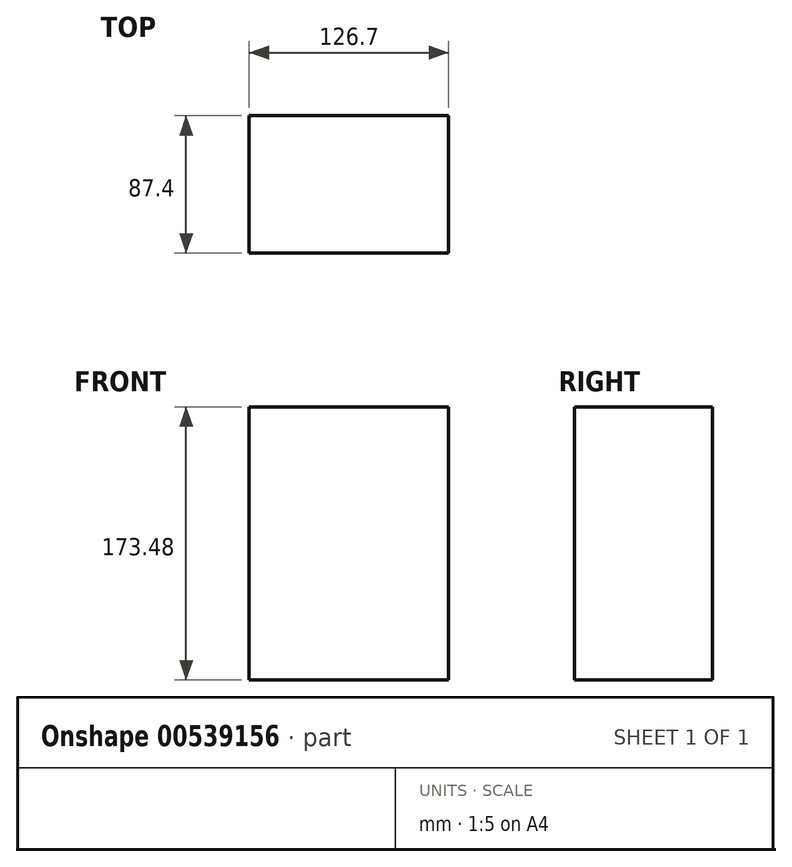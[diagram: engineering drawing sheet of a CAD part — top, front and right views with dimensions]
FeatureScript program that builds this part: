
annotation { "Feature Type Name" : "Feature", "Feature Type Description" : "" }
export const myFeature = defineFeature(function(context is Context, id is Id, definition is map)
    precondition{}
    {
        {
            var Q0;
            Q0=qCreatedBy(makeId("Top.planeOp"),FACE);
            var sketch = newSketch(context, id + "F0", { "sketchPlane" : qUnion([Q0])});
            skLineSegment(sketch, "E0.bottom", {"start": v(63.35, -43.7) * mm, "end": v(-63.35, -43.7) * mm});
            skLineSegment(sketch, "E0.top", {"start": v(63.35, 43.7) * mm, "end": v(-63.35, 43.7) * mm});
            skLineSegment(sketch, "E0.left", {"start": v(63.35, -43.7) * mm, "end": v(63.35, 43.7) * mm});
            skLineSegment(sketch, "E0.right", {"start": v(-63.35, -43.7) * mm, "end": v(-63.35, 43.7) * mm});
            skPoint(sketch, "E0.middle", {"position": v(0, 0) * mm});
            skSolve(sketch);
        }
        {
            var Q0;
            Q0 = qSketchRegion(id + "F0", true);
            extrude(context, id + "F1", {"entities" : qUnion([Q0]), "endBound" : BoundingType.SYMMETRIC, "depth" : 173.5 * mm, "offsetDistance" : 25.4 * mm});
        }
    });
